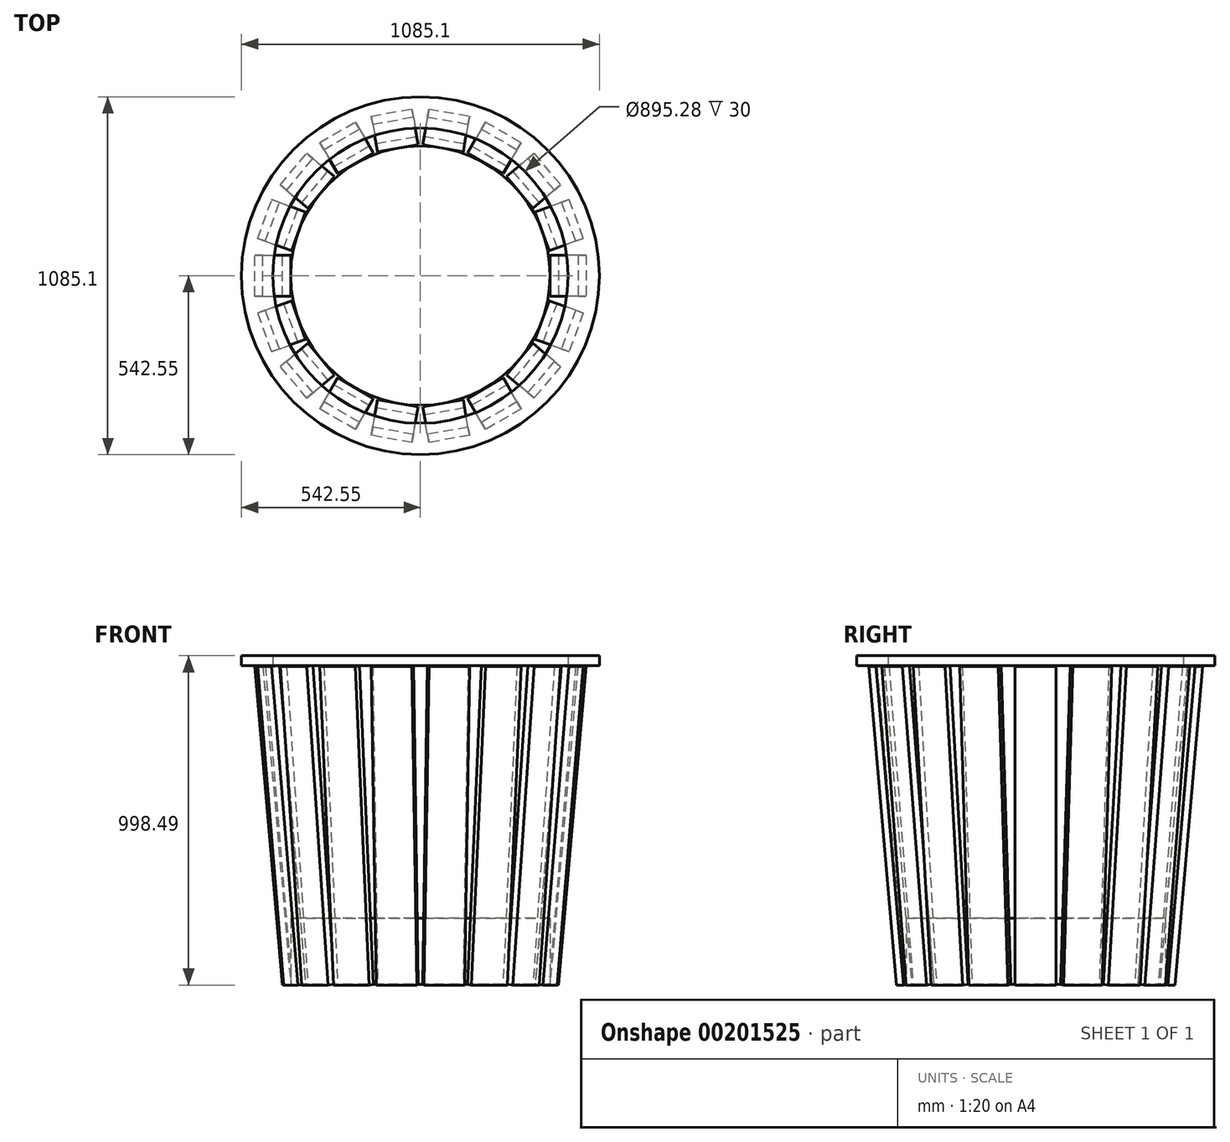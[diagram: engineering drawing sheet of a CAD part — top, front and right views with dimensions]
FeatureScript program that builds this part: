
annotation { "Feature Type Name" : "Feature", "Feature Type Description" : "" }
export const myFeature = defineFeature(function(context is Context, id is Id, definition is map)
    precondition{}
    {
        {
            var Q0;
            Q0=qCreatedBy(makeId("Top.planeOp"),FACE);
            var sketch = newSketch(context, id + "F0", { "sketchPlane" : qUnion([Q0])});
            skCircle(sketch, "E0", {"center": v(0, 0) * mm, "radius": 393.1 * mm});
            skLineSegment(sketch, "E1", {"start": v(0, 0) * mm, "end": v(-393.1, 0) * mm, "construction": true});
            skLineSegment(sketch, "E2.bottom", {"start": v(-393.1, -62.5) * mm, "end": v(-418.1, -62.5) * mm, "construction": true});
            skLineSegment(sketch, "E2.top", {"start": v(-393.1, 62.5) * mm, "end": v(-418.1, 62.5) * mm, "construction": true});
            skLineSegment(sketch, "E2.left", {"start": v(-393.1, -62.5) * mm, "end": v(-393.1, 62.5) * mm, "construction": true});
            skLineSegment(sketch, "E2.right", {"start": v(-418.1, -62.5) * mm, "end": v(-418.1, 62.5) * mm, "construction": true});
            skPoint(sketch, "E2.middle", {"position": v(-405.6, 0) * mm});
            skSolve(sketch);
        }
        {
            var Q0;
            Q0=makeQuery(id+"F0.imprint","IMPRINT",FACE,{"disambiguationData":[TD([[makeQuery(id+"F0.imprint","IMPRINT",EDGE,{"derivedFrom":sQuery(id+"F0.wireOp",EDGE,"E0")}),1.0]])]});
            extrude(context, id + "F1", {"entities" : qUnion([Q0]), "depth" : 200 * mm});
        }
        {
            var Q0;
            Q0=qCreatedBy(makeId("Top.planeOp"),FACE);
            var sketch = newSketch(context, id + "F2", { "sketchPlane" : qUnion([Q0])});
            skLineSegment(sketch, "E3.0", {"start": v(-393.1, -62.5) * mm, "end": v(-418.1, -62.5) * mm});
            skLineSegment(sketch, "E3.1", {"start": v(-418.1, -62.5) * mm, "end": v(-418.1, 62.5) * mm});
            skLineSegment(sketch, "E3.2", {"start": v(-393.1, -62.5) * mm, "end": v(-393.1, 62.5) * mm});
            skLineSegment(sketch, "E3.3", {"start": v(-393.1, 62.5) * mm, "end": v(-418.1, 62.5) * mm});
            skSolve(sketch);
        }
        {
            var Q0;
            Q0=makeQuery(id+"F2.imprint","IMPRINT",FACE,{"disambiguationData":[TD([[makeQuery(id+"F2.imprint","IMPRINT",EDGE,{"derivedFrom":sQuery(id+"F2.wireOp",EDGE,"E3.0")}),-1.0]])]});
            extrude(context, id + "F3", {"entities" : qUnion([Q0]), "depth" : (200 + 800 - 30) * mm});
        }
        {
            var Q0;
            Q0=makeQuery(id+"F3.opExtrude","SWEPT_BODY",BODY,{"disambiguationData":[OSD([sQuery(id+"F2.wireOp",EDGE,"E3.0"),sQuery(id+"F2.wireOp",EDGE,"E3.1"),sQuery(id+"F2.wireOp",EDGE,"E3.2"),sQuery(id+"F2.wireOp",EDGE,"E3.3")])]});
            var Q1;
            Q1=makeQuery(id+"F3.opExtrude","CAP_EDGE",EDGE,{"disambiguationData":[OSD([sQuery(id+"F2.wireOp",EDGE,"E3.2")])],"isStart":true});
            transform(context, id + "F4", {"entities" : qUnion([Q0]), "transformType" : TransformType.ROTATION, "transformAxis" : qUnion([Q1]), "angle" : 5 * degree, "oppositeDirection" : true, "makeCopy" : false});
        }
        {
            var Q0;
            Q0=makeQuery(id+"F3.opExtrude","SWEPT_BODY",BODY,{"disambiguationData":[OSD([sQuery(id+"F2.wireOp",EDGE,"E3.0"),sQuery(id+"F2.wireOp",EDGE,"E3.1"),sQuery(id+"F2.wireOp",EDGE,"E3.2"),sQuery(id+"F2.wireOp",EDGE,"E3.3")])]});
            var Q1;
            Q1=makeQuery(id+"F1.opExtrude","SWEPT_FACE",FACE,{"disambiguationData":[OSD([sQuery(id+"F0.wireOp",EDGE,"E0")])]});
            circularPattern(context, id + "F5", {"entities" : qUnion([Q0]), "axis" : qUnion([Q1]), "angle" : 360 * degree, "instanceCount" : 18, "equalSpace" : true});
        }
        {
            var Q0;
            Q0=makeQuery(id+"F5.opPattern","COPY",VERTEX,{"derivedFrom":makeQuery(id+"F3.opExtrude","CAP_VERTEX",VERTEX,{"disambiguationData":[OSD([sQuery(id+"F2.wireOp",EDGE,"E3.2"),sQuery(id+"F2.wireOp",EDGE,"E3.3")])],"isStart":false}),"instanceName":"6"});
            var Q1;
            Q1=makeQuery(id+"F5.opPattern","COPY",VERTEX,{"derivedFrom":makeQuery(id+"F3.opExtrude","CAP_VERTEX",VERTEX,{"disambiguationData":[OSD([sQuery(id+"F2.wireOp",EDGE,"E3.0"),sQuery(id+"F2.wireOp",EDGE,"E3.2")])],"isStart":false}),"instanceName":"17"});
            var Q2;
            Q2=makeQuery(id+"F5.opPattern","COPY",VERTEX,{"derivedFrom":makeQuery(id+"F3.opExtrude","CAP_VERTEX",VERTEX,{"disambiguationData":[OSD([sQuery(id+"F2.wireOp",EDGE,"E3.0"),sQuery(id+"F2.wireOp",EDGE,"E3.2")])],"isStart":false}),"instanceName":"10"});
            cPlane(context, id + "F6", {"entities" : qUnion([Q0, Q1, Q2]), "cplaneType" : CPlaneType.THREE_POINT, "offset" : 25 * mm, "width" : 150 * mm, "height" : 150 * mm});
        }
        {
            var Q0;
            Q0=qCreatedBy(id+"F6.planeOp",FACE);
            var sketch = newSketch(context, id + "F7", { "sketchPlane" : qUnion([Q0])});
            skCircle(sketch, "E4", {"center": v(0, 0) * mm, "radius": 447.64 * mm});
            skCircle(sketch, "E5", {"center": v(0, 0) * mm, "radius": 542.55 * mm});
            skSolve(sketch);
        }
        {
            var Q0;
            Q0=makeQuery(id+"F7.imprint","IMPRINT",FACE,{"disambiguationData":[TD([[makeQuery(id+"F7.imprint","IMPRINT",EDGE,{"derivedFrom":sQuery(id+"F7.wireOp",EDGE,"E4")}),-1.0]])]});
            extrude(context, id + "F8", {"entities" : qUnion([Q0]), "oppositeDirection" : true, "depth" : 30 * mm});
        }
    });
